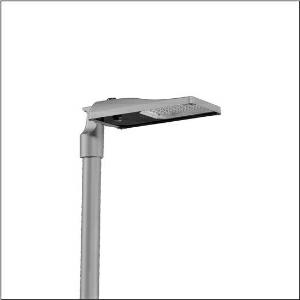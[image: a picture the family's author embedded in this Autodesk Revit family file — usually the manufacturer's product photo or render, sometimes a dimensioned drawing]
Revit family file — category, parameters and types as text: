
# Revit family: streetlight_sl_31_mini___st1_0a_5xh6d31t08ga_3ef0
name_source: partatom
category: Lighting Fixtures
units: mm (PartAtom-declared; Revit-internal decimal feet)

## family parameters
Cut with Voids When Loaded = No
Host = Face
Light Source = No
Part Type = Normal
Room Calculation Point = No
Round Connector Dimension = Use Diameter
Shared = No

## types (1)
- --- (1 x LED, 5880 lm, 39.3 W, 3000K)
    Apparent Load = 39 VA
    CIE Flux Codes = 37 72 97 100 100
    Color Rendering = 70
    Color Temperature = 3000K
    Default Elevation = 1800 mm
    Description = Streetlight SL 31 mini D4i, Desk-Remote mast luminaire for post-top, side-entry; light control with lens of PMMA; light distribution: ST1.0a, direct asymmetric distribution, for standard-compliant lighting for roads and squares; LED: luminous flux: 5.880lm, light colour: 730, colour temperature: 3000K; luminous efficacy: 149,6lm/W; control: pre-setting: logarithmic dimming characteristic, flexible luminous flux parameterisation, time-dependent luminous flux control, constant luminous flux control, power reduction, intelligent temperature release in ECG and LED module, overheat protection; luminaire housing, of diecast aluminium, SITECO metallic grey (DB 702S), corrosivity category C5 high according to DIN EN ISO 12944; cover of toughened safety glass, transparent, opened without tools; mast flange of diecast aluminium, SITECO metallic grey (DB 702S), spigot size: 76/60mm, mast flange included unmounted; with cable H07RN-F 2x 1.5mm², cable length: 6,5m, connection cable pre-assembled; mains connection: 220..240V, AC, 50/60Hz; power consumption (at start of service life): 39,3W / (at end of service life): 40,7W / (with reduced operation 50%): 18,1W; protection rating (complete): IP66; insulation class (complete): insulation class II (safety insulation); impact resistance: IK09; certification: CE, ENEC, ENEC+, VDE, UKCA, ZD4i; permissible operating ambient temperature for outdoor applications: -40..+50°C; packaging unit: 1 piece

Light Distribution: ST1.0a
    Height = 76 mm
    Lamp = 1 x LED
    Lamp Light Flux = 5880 lm
    Lamp Power = 39.3 W
    Lamp count = 1
    Length = 547 mm
    Luminous efficacy = 150 lm/W
    Manufacturer = Siteco
    ModVariant = No
    Model = 5XH6D31T08GA
    Number of Poles = 1
    OnlyDefault = Yes
    Power Factor = 1
    Product Name = Streetlight SL 31 mini | ST1.0a
    Product group = mast luminaire | pylon top
    ProductGroupID = 6100
    Protection Class = Protection class II
    Protection Degree = IP 66
    RLX_Detail_Level = 1
    RLX_Emergency_Light_Flux = 0 lm
    RLX_Emergency_Type = 0
    RLX_Emergency_Type_DB = No
    RlxData = <blob elided: 39701 chars, md5=4534bec0>
    Socket = socket
    Standby Power = 0 W
    System Light Flux = 5880 lm
    System Power = 39 W
    Type Comments = factory setting: luminous flux: 100 % | dim-lin: 254 | 798 mA
    Type Image = l_1300332.jpg
    URL = http://relux.com
    VarID = @adj_060625
    Voltage = 0 V
    Weight = 0.00 kg
    Width = 265 mm

## geometry (parser evidence)
native form markers: Blend x4, Sweep x8
no freeform markers — native parametric forms only
